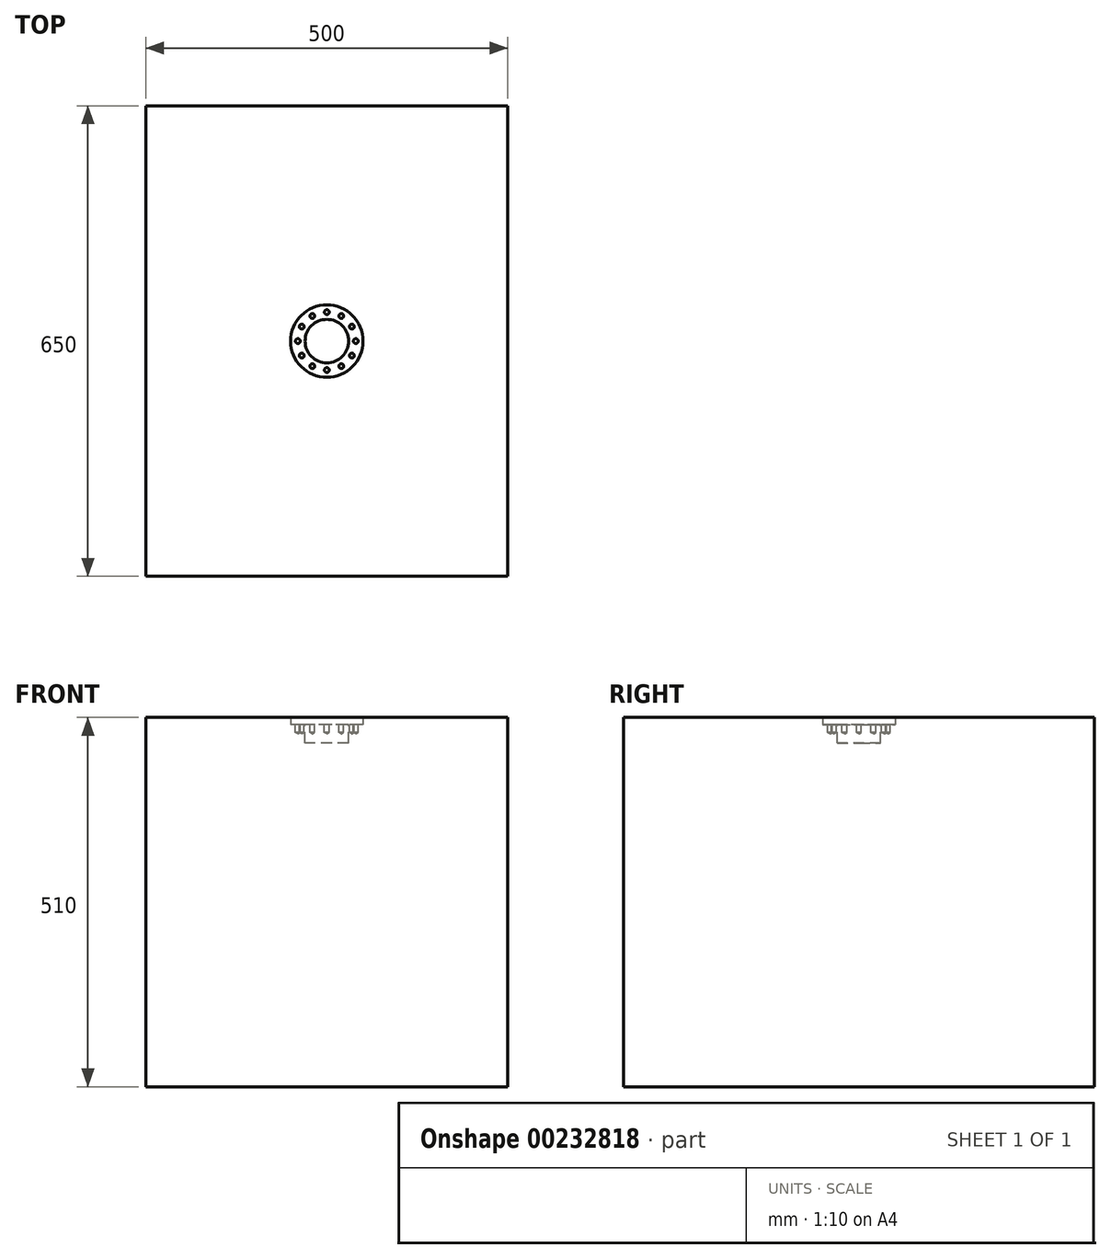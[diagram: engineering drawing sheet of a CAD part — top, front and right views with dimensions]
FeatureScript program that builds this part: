
annotation { "Feature Type Name" : "Feature", "Feature Type Description" : "" }
export const myFeature = defineFeature(function(context is Context, id is Id, definition is map)
    precondition{}
    {
        {
            var Q0;
            Q0=qCreatedBy(makeId("Front.planeOp"),FACE);
            var sketch = newSketch(context, id + "F0", { "sketchPlane" : qUnion([Q0])});
            skLineSegment(sketch, "E0.bottom", {"start": v(250, -250) * mm, "end": v(-250, -250) * mm});
            skLineSegment(sketch, "E0.top", {"start": v(250, 250) * mm, "end": v(-250, 250) * mm});
            skLineSegment(sketch, "E0.left", {"start": v(250, -250) * mm, "end": v(250, 250) * mm});
            skLineSegment(sketch, "E0.right", {"start": v(-250, -250) * mm, "end": v(-250, 250) * mm});
            skPoint(sketch, "E0.middle", {"position": v(0, 0) * mm});
            skSolve(sketch);
        }
        {
            var Q0;
            Q0 = qSketchRegion(id + "F0", true);
            extrude(context, id + "F1", {"entities" : qUnion([Q0]), "endBound" : BoundingType.SYMMETRIC, "depth" : 650 * mm});
        }
        {
            var Q0;
            Q0=makeQuery(id+"F1.opExtrude","SWEPT_FACE",FACE,{"disambiguationData":[OSD([sQuery(id+"F0.wireOp",EDGE,"E0.top")])]});
            var sketch = newSketch(context, id + "F2", { "sketchPlane" : qUnion([Q0])});
            skCircle(sketch, "E1", {"center": v(0, 0) * mm, "radius": 50 * mm});
            skCircle(sketch, "E2", {"center": v(0, 0) * mm, "radius": 30 * mm});
            skSolve(sketch);
        }
        {
            var Q0;
            Q0=makeQuery(id+"F2.imprint","IMPRINT",FACE,{"disambiguationData":[TD([[makeQuery(id+"F2.imprint","IMPRINT",EDGE,{"derivedFrom":sQuery(id+"F2.wireOp",EDGE,"E1")}),-1.0]])]});
            extrude(context, id + "F3", {"entities" : qUnion([Q0]), "operationType" : NewBodyOperationType.ADD, "depth" : 10 * mm});
        }
        {
            var Q0;
            Q0=makeQuery(id+"F2.imprint","IMPRINT",FACE,{"disambiguationData":[TD([[makeQuery(id+"F2.imprint","IMPRINT",EDGE,{"derivedFrom":sQuery(id+"F2.wireOp",EDGE,"E2")}),1.0]])]});
            extrude(context, id + "F4", {"entities" : qUnion([Q0]), "operationType" : NewBodyOperationType.REMOVE, "oppositeDirection" : true, "depth" : 25 * mm});
        }
        {
            var Q0;
            Q0=makeQuery(id+"F2.imprint","IMPRINT",FACE,{"disambiguationData":[TD([[makeQuery(id+"F2.imprint","IMPRINT",EDGE,{"derivedFrom":sQuery(id+"F2.wireOp",EDGE,"E1")}),1.0]])]});
            var sketch = newSketch(context, id + "F5", { "sketchPlane" : qUnion([Q0])});
            skPoint(sketch, "E3", {"position": v(0, 40) * mm});
            skPoint(sketch, "E4.1.0", {"position": v(-20, 34.64) * mm});
            skPoint(sketch, "E4.2.0", {"position": v(-34.64, 20) * mm});
            skPoint(sketch, "E4.3.0", {"position": v(-40, 0) * mm});
            skPoint(sketch, "E4.4.0", {"position": v(-34.64, -20) * mm});
            skPoint(sketch, "E4.5.0", {"position": v(-20, -34.64) * mm});
            skPoint(sketch, "E4.6.0", {"position": v(0, -40) * mm});
            skPoint(sketch, "E4.7.0", {"position": v(20, -34.64) * mm});
            skPoint(sketch, "E4.8.0", {"position": v(34.64, -20) * mm});
            skPoint(sketch, "E4.9.0", {"position": v(40, 0) * mm});
            skPoint(sketch, "E4.10.0", {"position": v(34.64, 20) * mm});
            skPoint(sketch, "E4.11.0", {"position": v(20, 34.64) * mm});
            skPoint(sketch, "E4.center", {"position": v(0, 0) * mm});
            skSolve(sketch);
        }
        {
            var Q0;
            Q0=sQuery(id+"F5.wireOp",VERTEX,"E4.5.0");
            var Q1;
            Q1=sQuery(id+"F5.wireOp",VERTEX,"E4.10.0");
            var Q2;
            Q2=sQuery(id+"F5.wireOp",VERTEX,"E4.2.0");
            var Q3;
            Q3=sQuery(id+"F5.wireOp",VERTEX,"E4.1.0");
            var Q4;
            Q4=sQuery(id+"F5.wireOp",VERTEX,"E3");
            var Q5;
            Q5=sQuery(id+"F5.wireOp",VERTEX,"E4.7.0");
            var Q6;
            Q6=sQuery(id+"F5.wireOp",VERTEX,"E4.3.0");
            var Q7;
            Q7=sQuery(id+"F5.wireOp",VERTEX,"E4.11.0");
            var Q8;
            Q8=sQuery(id+"F5.wireOp",VERTEX,"E4.4.0");
            var Q9;
            Q9=sQuery(id+"F5.wireOp",VERTEX,"E4.8.0");
            var Q10;
            Q10=sQuery(id+"F5.wireOp",VERTEX,"E4.9.0");
            var Q11;
            Q11=sQuery(id+"F5.wireOp",VERTEX,"E4.6.0");
            var Q12;
            Q12=sQuery(id+"F2.wireOp",VERTEX,"E2.center");
            var Q13;
            Q13=sQuery(id+"F5.wireOp",VERTEX,"E4.center");
            var Q14;
            Q14=makeQuery(id+"F1.opExtrude","SWEPT_BODY",BODY,{"disambiguationData":[OSD([sQuery(id+"F0.wireOp",EDGE,"E0.bottom"),sQuery(id+"F0.wireOp",EDGE,"E0.top"),sQuery(id+"F0.wireOp",EDGE,"E0.left"),sQuery(id+"F0.wireOp",EDGE,"E0.right")])]});
            hole(context, id + "F6", {"style" : HoleStyle.SIMPLE, "endStyle" : HoleEndStyle.BLIND, "standardTappedOrClearance" : lookupTablePath({ "standard" : "ISO", "fit" : "Normal", "size" : "M6", "type" : "Clearance" }), "standardBlindInLast" : lookupTablePath({ "fit" : "Standard", "standard" : "ISO", "size" : "M6", "type" : "Clearance" }), "holeDiameter" : 6.6 * mm, "holeDepth" : 10.5 * mm, "tappedDepth" : 32 * mm, "tapClearance" : 3, "startFromSketch" : true, "locations" : qUnion([Q0, Q1, Q2, Q3, Q4, Q5, Q6, Q7, Q8, Q9, Q10, Q11, Q12, Q13]), "scope" : qUnion([Q14])});
        }
    });
